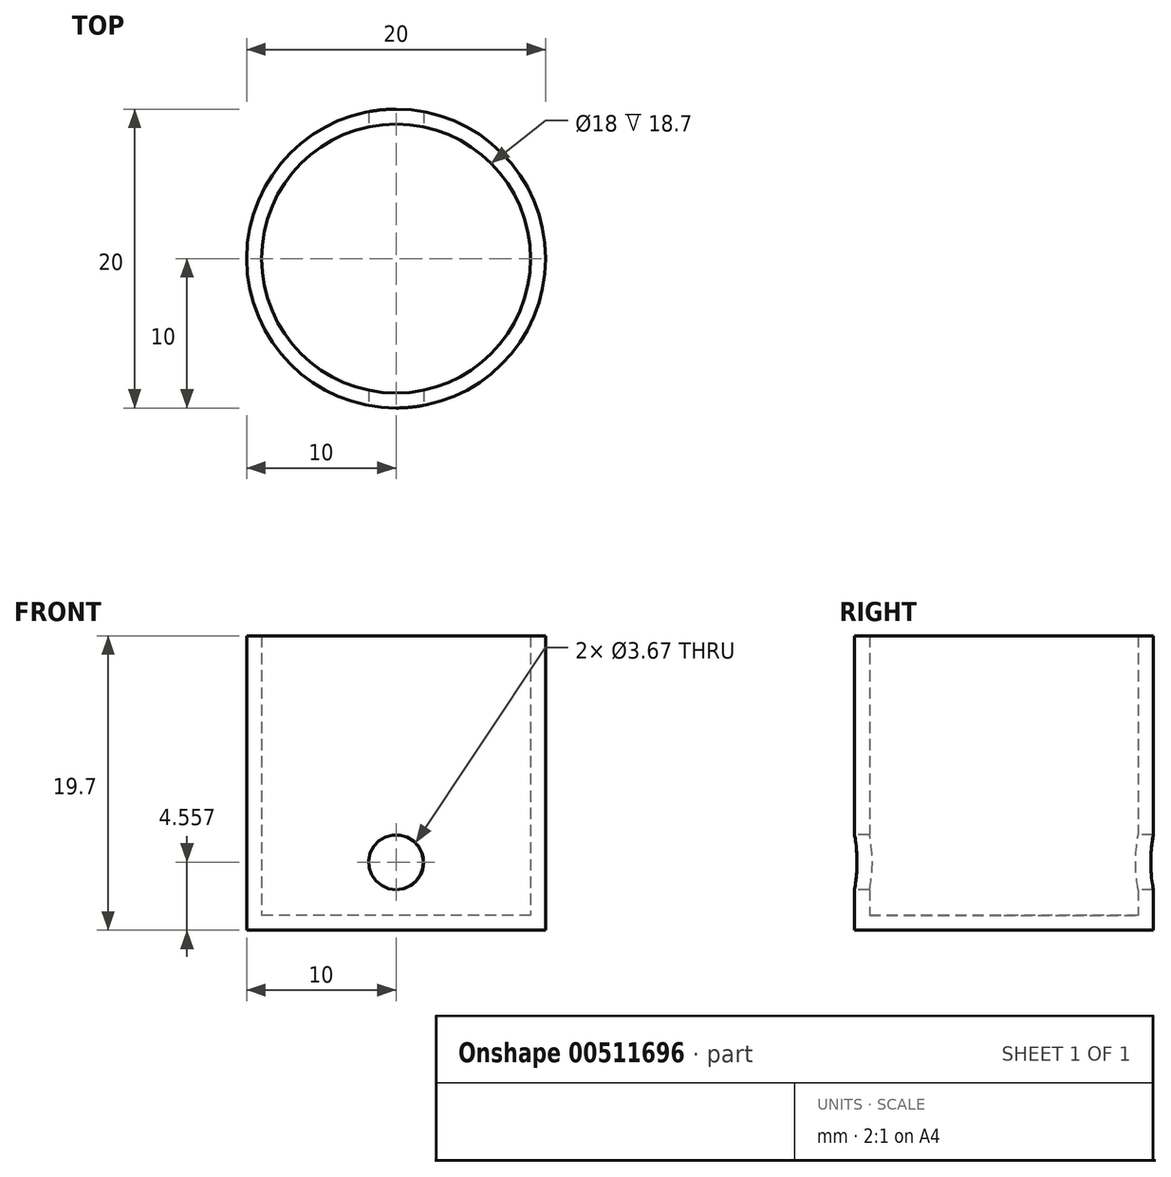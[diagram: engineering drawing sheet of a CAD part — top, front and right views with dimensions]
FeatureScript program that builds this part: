
annotation { "Feature Type Name" : "Feature", "Feature Type Description" : "" }
export const myFeature = defineFeature(function(context is Context, id is Id, definition is map)
    precondition{}
    {
        {
            var Q0;
            Q0=qCreatedBy(makeId("Top.planeOp"),FACE);
            var sketch = newSketch(context, id + "F0", { "sketchPlane" : qUnion([Q0])});
            skCircle(sketch, "E0", {"center": v(0, 0) * mm, "radius": 10 * mm});
            skSolve(sketch);
        }
        {
            var Q0;
            Q0 = qSketchRegion(id + "F0", true);
            extrude(context, id + "F1", {"entities" : qUnion([Q0]), "depth" : 19.7 * mm, "offsetDistance" : 25 * mm});
        }
        {
            var Q0;
            Q0=makeQuery(id+"F1.opExtrude","CAP_FACE",FACE,{"disambiguationData":[OSD([sQuery(id+"F0.wireOp",EDGE,"E0")])],"isStart":false});
            shell(context, id + "F2", {"entities" : qUnion([Q0]), "thickness" : 1 * mm});
        }
        {
            var Q0;
            Q0=qCreatedBy(makeId("Front.planeOp"),FACE);
            var sketch = newSketch(context, id + "F3", { "sketchPlane" : qUnion([Q0])});
            skCircle(sketch, "E1", {"center": v(0, 4.56) * mm, "radius": 1.84 * mm});
            skSolve(sketch);
        }
        {
            var Q0;
            Q0 = qSketchRegion(id + "F3", true);
            extrude(context, id + "F4", {"entities" : qUnion([Q0]), "operationType" : NewBodyOperationType.REMOVE, "endBound" : BoundingType.SYMMETRIC, "oppositeDirection" : true, "depth" : 23.2 * mm, "offsetDistance" : 25 * mm});
        }
    });
